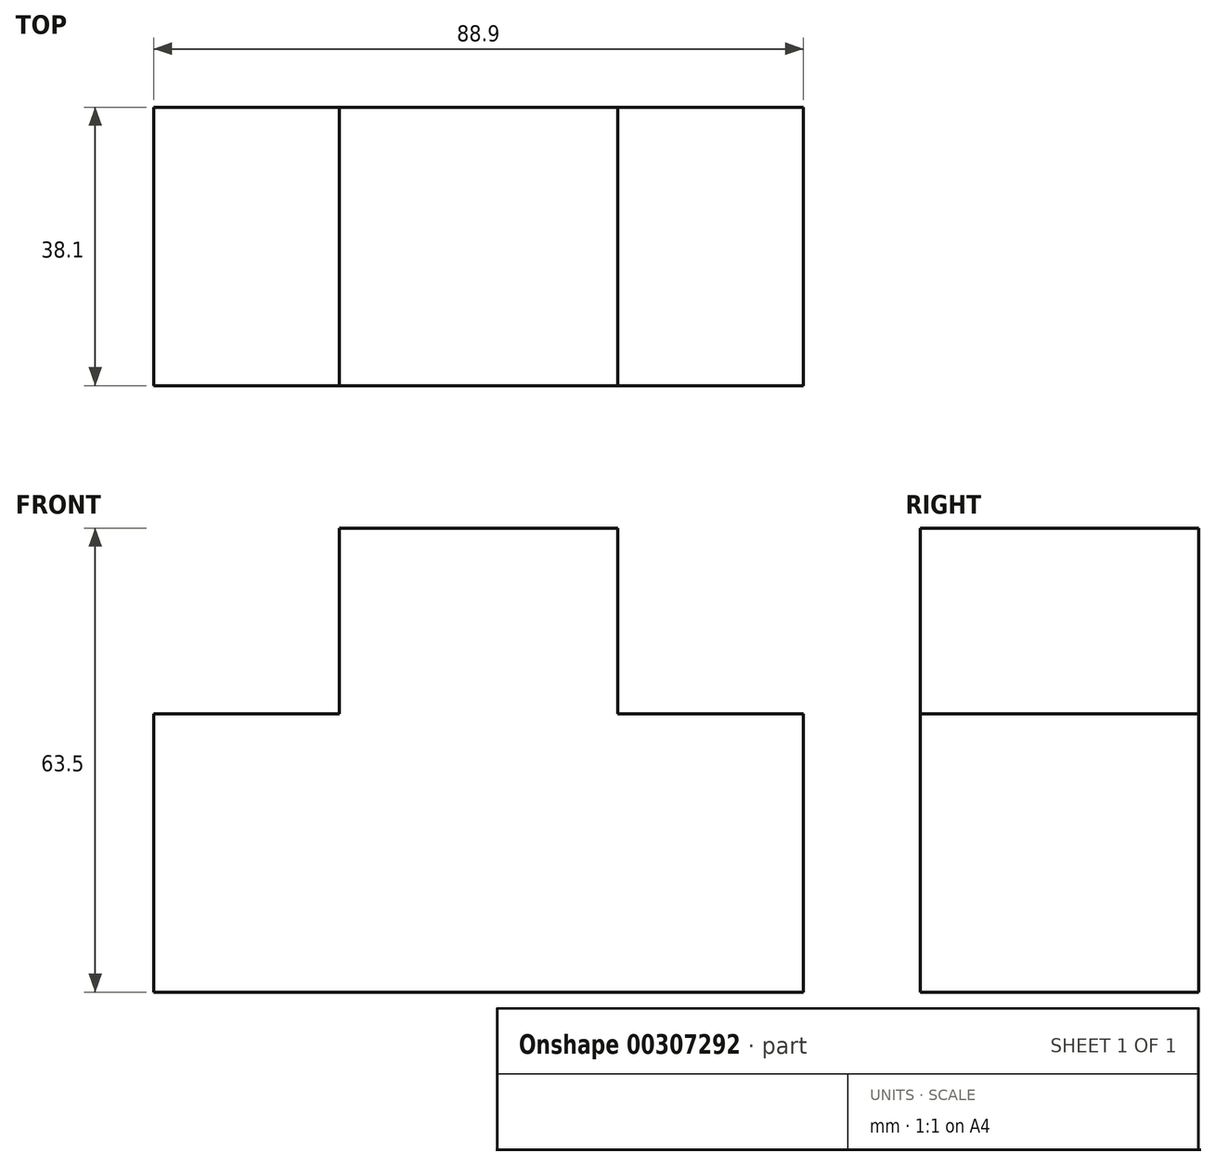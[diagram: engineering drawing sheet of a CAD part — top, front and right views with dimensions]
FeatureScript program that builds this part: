
annotation { "Feature Type Name" : "Feature", "Feature Type Description" : "" }
export const myFeature = defineFeature(function(context is Context, id is Id, definition is map)
    precondition{}
    {
        {
            var Q0;
            Q0=qCreatedBy(makeId("Front.planeOp"),FACE);
            var sketch = newSketch(context, id + "F0", { "sketchPlane" : qUnion([Q0])});
            skLineSegment(sketch, "E0", {"start": v(-28.64, -36.58) * mm, "end": v(60.26, -36.58) * mm});
            skLineSegment(sketch, "E1", {"start": v(60.26, -36.58) * mm, "end": v(60.26, 1.52) * mm});
            skLineSegment(sketch, "E2", {"start": v(60.26, 1.52) * mm, "end": v(34.86, 1.52) * mm});
            skLineSegment(sketch, "E3", {"start": v(34.86, 1.52) * mm, "end": v(34.86, 26.92) * mm});
            skLineSegment(sketch, "E4", {"start": v(34.86, 26.92) * mm, "end": v(-3.24, 26.92) * mm});
            skLineSegment(sketch, "E5", {"start": v(-3.24, 26.92) * mm, "end": v(-3.24, 1.52) * mm});
            skLineSegment(sketch, "E6", {"start": v(-3.24, 1.52) * mm, "end": v(-28.64, 1.52) * mm});
            skLineSegment(sketch, "E7", {"start": v(-28.64, 1.52) * mm, "end": v(-28.64, -36.58) * mm});
            skSolve(sketch);
        }
        {
            var Q0;
            Q0=makeQuery(id+"F0.imprint","IMPRINT",FACE,{"disambiguationData":[TD([[makeQuery(id+"F0.imprint","IMPRINT",EDGE,{"derivedFrom":sQuery(id+"F0.wireOp",EDGE,"E0")}),1.0]])]});
            extrude(context, id + "F1", {"entities" : qUnion([Q0]), "depth" : 38.1 * mm});
        }
    });
